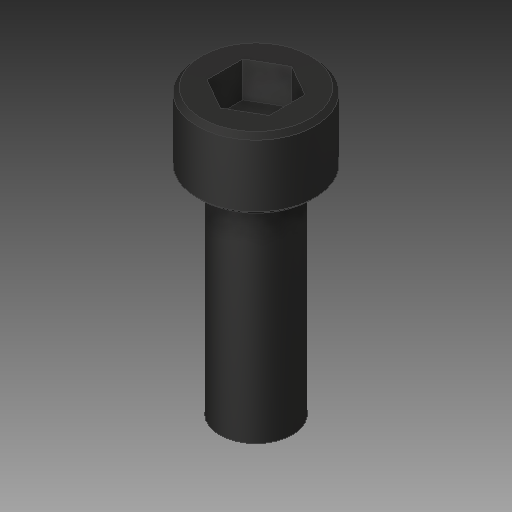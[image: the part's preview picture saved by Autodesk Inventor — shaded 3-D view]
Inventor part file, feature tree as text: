
AUTODESK INVENTOR PART (.ipt)
format: ipt  version: 2017 (Build 210142000, 142)  size: 104,960 bytes
history: native  units: in
note: dims shown in document units (in); Inventor stores cm internally (conversion verified against a paired STEP export)
features: chamfer x1
ambient origin geometry x8: Origin, YZ Plane, XZ Plane, XY Plane, X Axis, Y Axis, Z Axis, Center Point
bodies: Solid1 (feature_tree)
feature tree (1):
  chamfer  "Chamfer2"  [1 undecoded]
note: 1 required parameter value undecoded (feature->parameter linkage not recoverable at this tier; creation-order binding heuristic only, values carry confidence <= 0.55)
